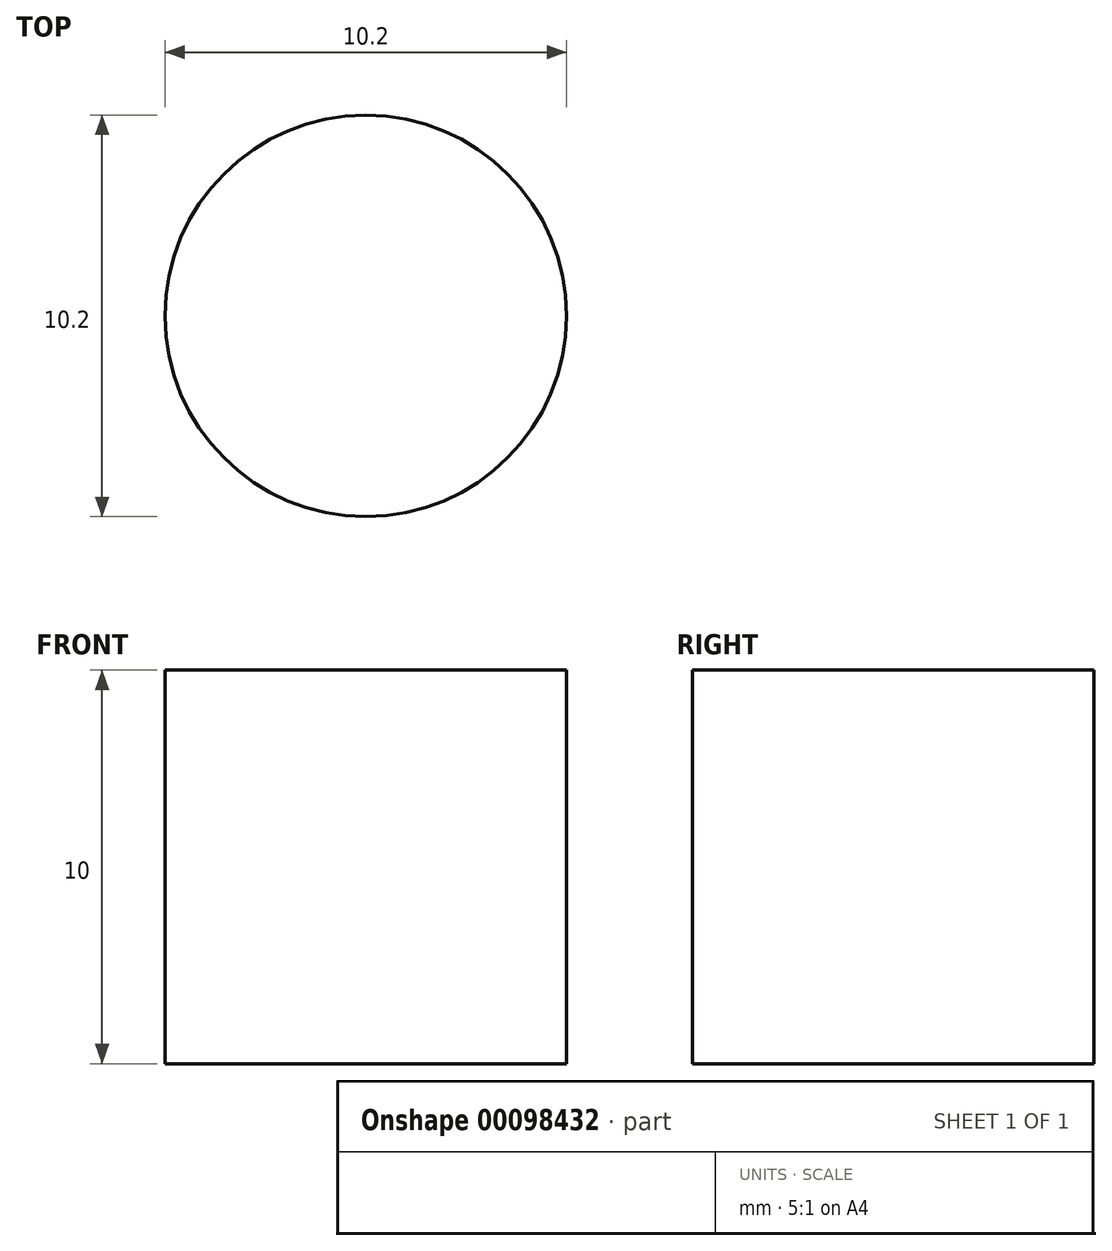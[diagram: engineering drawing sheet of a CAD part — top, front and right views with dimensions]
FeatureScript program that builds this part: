
annotation { "Feature Type Name" : "Feature", "Feature Type Description" : "" }
export const myFeature = defineFeature(function(context is Context, id is Id, definition is map)
    precondition{}
    {
        {
            var Q0;
            Q0=qCreatedBy(makeId("Top.planeOp"),FACE);
            var sketch = newSketch(context, id + "F0", { "sketchPlane" : qUnion([Q0])});
            skCircle(sketch, "E0", {"center": v(0, 0) * mm, "radius": 5.1 * mm});
            skSolve(sketch);
        }
        {
            var Q0;
            Q0 = qSketchRegion(id + "F0", true);
            extrude(context, id + "F1", {"entities" : qUnion([Q0]), "depth" : 10 * mm});
        }
    });
